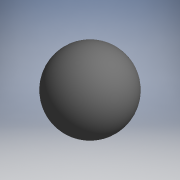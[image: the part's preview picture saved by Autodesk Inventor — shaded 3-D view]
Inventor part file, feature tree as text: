
AUTODESK INVENTOR PART (.ipt)
format: ipt  version: 2017.3 (Build 213256000, 256)  size: 111,104 bytes
history: native  units: mm (DEFAULTED — no unit token found)
features: other x7, revolve x1, sketch x1
ambient origin geometry x8: Origin, YZ Plane, XZ Plane, XY Plane, X Axis, Y Axis, Z Axis, Center Point
bodies: Solid1 (feature_tree)
feature tree (9):
  revolve  "Revolution1"  [1 undecoded]
  other  "ip_op_b_XY"
  other  "ip_op_b_YZ"
  other  "ip_op_b_ZX"
  other  "ip_op_b_X"
  other  "ip_op_b_Y"
  other  "ip_op_b_Z"
  other  "ip_op_b_Center"
  sketch  "Sketch_1"  dims[d0=360.0deg]
note: 1 required parameter value undecoded (feature->parameter linkage not recoverable at this tier; creation-order binding heuristic only, values carry confidence <= 0.55)
